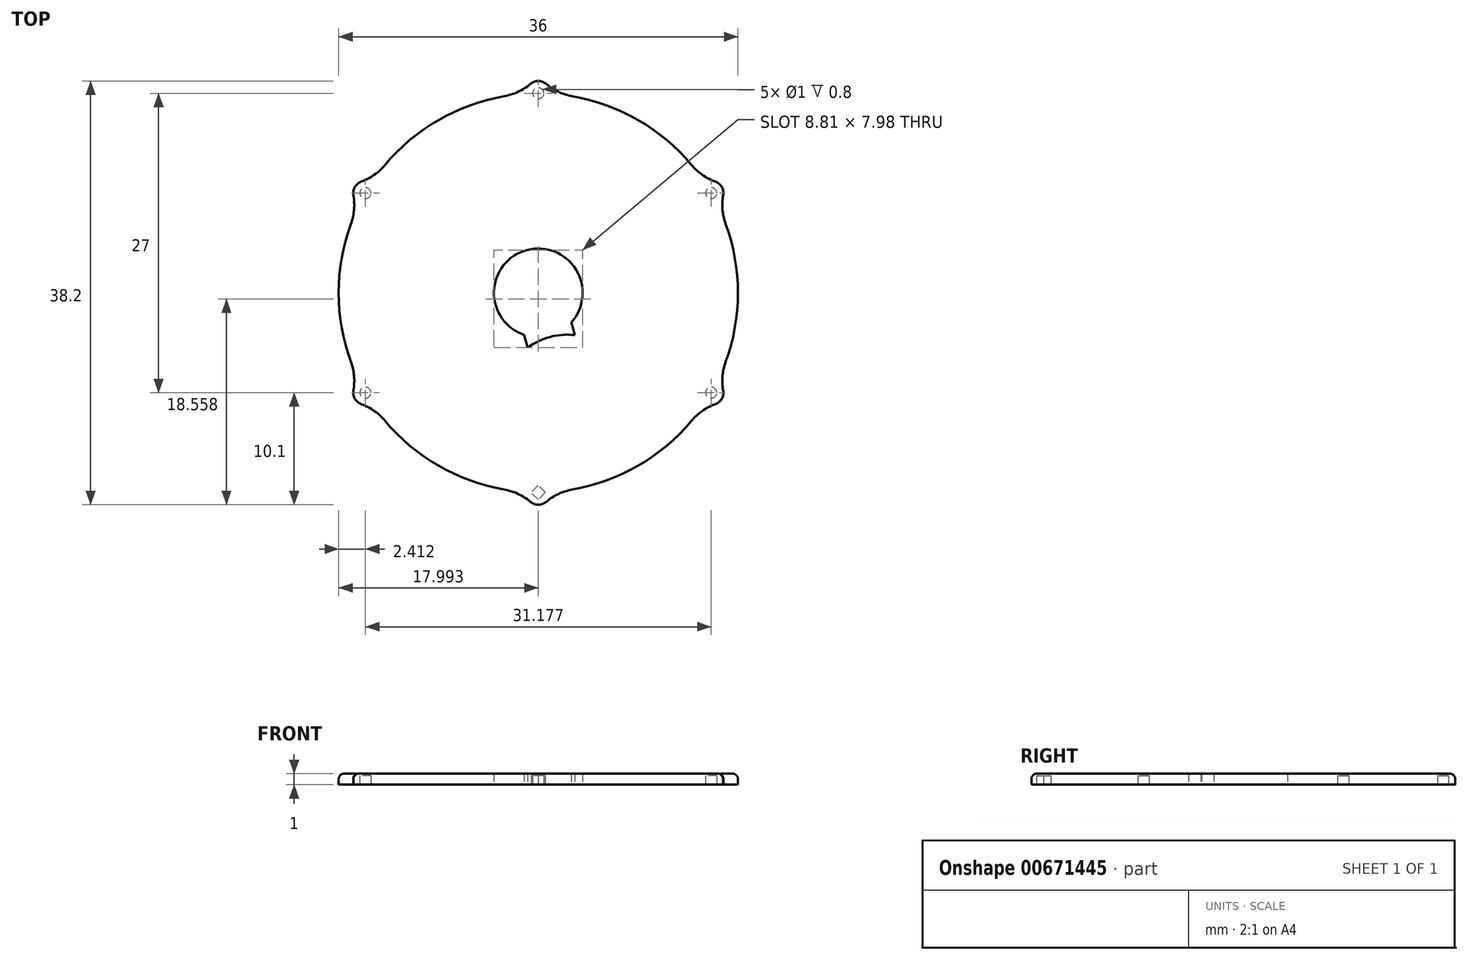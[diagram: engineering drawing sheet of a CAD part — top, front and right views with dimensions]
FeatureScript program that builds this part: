
annotation { "Feature Type Name" : "Feature", "Feature Type Description" : "" }
export const myFeature = defineFeature(function(context is Context, id is Id, definition is map)
    precondition{}
    {
        {
            var Q0;
            Q0=qCreatedBy(makeId("Top.planeOp"),FACE);
            var sketch = newSketch(context, id + "F0", { "sketchPlane" : qUnion([Q0])});
            skCircle(sketch, "E0", {"center": v(0, 0) * mm, "radius": 18 * mm});
            skCircle(sketch, "E1.0", {"center": v(0, 0) * mm, "radius": 17 * mm});
            skLineSegment(sketch, "E2.bottom", {"start": v(8.56, 15.83) * mm, "end": v(9.43, 15.33) * mm});
            skLineSegment(sketch, "E2.top", {"start": v(-9.43, -15.33) * mm, "end": v(-8.56, -15.83) * mm});
            skLineSegment(sketch, "E2.left", {"start": v(8.56, 15.83) * mm, "end": v(-9.43, -15.33) * mm});
            skLineSegment(sketch, "E2.right", {"start": v(9.43, 15.33) * mm, "end": v(-8.56, -15.83) * mm});
            skLineSegment(sketch, "E3.bottom", {"start": v(15.33, 9.43) * mm, "end": v(15.83, 8.56) * mm});
            skLineSegment(sketch, "E3.top", {"start": v(-15.83, -8.56) * mm, "end": v(-15.33, -9.43) * mm});
            skLineSegment(sketch, "E3.left", {"start": v(15.33, 9.43) * mm, "end": v(-15.83, -8.56) * mm});
            skLineSegment(sketch, "E3.right", {"start": v(15.83, 8.56) * mm, "end": v(-15.33, -9.43) * mm});
            skLineSegment(sketch, "E4", {"start": v(-38.35, 0) * mm, "end": v(39.17, 0) * mm, "construction": true});
            skLineSegment(sketch, "E5", {"start": v(0, 42.5) * mm, "end": v(0, -42.47) * mm, "construction": true});
            skLineSegment(sketch, "E6.bottom", {"start": v(-18, 0.5) * mm, "end": v(18, 0.5) * mm});
            skLineSegment(sketch, "E6.top", {"start": v(-18, -0.5) * mm, "end": v(18, -0.5) * mm});
            skLineSegment(sketch, "E6.left", {"start": v(-18, 0.5) * mm, "end": v(-18, -0.5) * mm});
            skLineSegment(sketch, "E6.right", {"start": v(18, 0.5) * mm, "end": v(18, -0.5) * mm});
            skLineSegment(sketch, "E7.bottom", {"start": v(-15.33, 9.43) * mm, "end": v(15.83, -8.56) * mm});
            skLineSegment(sketch, "E7.top", {"start": v(-15.83, 8.56) * mm, "end": v(15.33, -9.43) * mm});
            skLineSegment(sketch, "E7.left", {"start": v(-15.33, 9.43) * mm, "end": v(-15.83, 8.56) * mm});
            skLineSegment(sketch, "E7.right", {"start": v(15.83, -8.56) * mm, "end": v(15.33, -9.43) * mm});
            skLineSegment(sketch, "E8.bottom", {"start": v(-0.5, 18) * mm, "end": v(0.5, 18) * mm});
            skLineSegment(sketch, "E8.top", {"start": v(-0.5, -18) * mm, "end": v(0.5, -18) * mm});
            skLineSegment(sketch, "E8.left", {"start": v(-0.5, 18) * mm, "end": v(-0.5, -18) * mm});
            skLineSegment(sketch, "E8.right", {"start": v(0.5, 18) * mm, "end": v(0.5, -18) * mm});
            skLineSegment(sketch, "E9.bottom", {"start": v(-9.43, 15.33) * mm, "end": v(-8.56, 15.83) * mm});
            skLineSegment(sketch, "E9.top", {"start": v(8.56, -15.83) * mm, "end": v(9.43, -15.33) * mm});
            skLineSegment(sketch, "E9.left", {"start": v(-9.43, 15.33) * mm, "end": v(8.56, -15.83) * mm});
            skLineSegment(sketch, "E9.right", {"start": v(-8.56, 15.83) * mm, "end": v(9.43, -15.33) * mm});
            skCircle(sketch, "E10", {"center": v(0, 0) * mm, "radius": 13.47 * mm});
            skSolve(sketch);
        }
        {
            var Q0;
            Q0=qCreatedBy(makeId("Top.planeOp"),FACE);
            var sketch = newSketch(context, id + "F1", { "sketchPlane" : qUnion([Q0])});
            skCircle(sketch, "E11", {"center": v(0, 0) * mm, "radius": 18 * mm});
            skCircle(sketch, "E12", {"center": v(0, 0) * mm, "radius": 17 * mm});
            skSolve(sketch);
        }
        {
            var Q0;
            Q0=makeQuery(id+"F1.imprint","IMPRINT",FACE,{"disambiguationData":[TD([[makeQuery(id+"F1.imprint","IMPRINT",EDGE,{"derivedFrom":sQuery(id+"F1.wireOp",EDGE,"E11")}),1.0]])]});
            extrude(context, id + "F2", {"entities" : qUnion([Q0]), "depth" : 1 * mm, "offsetDistance" : 25 * mm});
        }
        {
            var Q0;
            Q0=makeQuery(id+"F1.imprint","IMPRINT",FACE,{"disambiguationData":[TD([[makeQuery(id+"F1.imprint","IMPRINT",EDGE,{"derivedFrom":sQuery(id+"F1.wireOp",EDGE,"E11")}),1.0]])]});
            var Q1;
            Q1=makeQuery(id+"F1.imprint","IMPRINT",FACE,{"disambiguationData":[TD([[makeQuery(id+"F1.imprint","IMPRINT",EDGE,{"derivedFrom":sQuery(id+"F1.wireOp",EDGE,"E12")}),1.0]])]});
            extrude(context, id + "F3", {"entities" : qUnion([Q0, Q1]), "operationType" : NewBodyOperationType.ADD, "depth" : 1 * mm, "offsetDistance" : 25 * mm});
        }
        {
            var Q0;
            Q0=qCreatedBy(makeId("Top.planeOp"),FACE);
            var sketch = newSketch(context, id + "F4", { "sketchPlane" : qUnion([Q0])});
            skCircle(sketch, "E13", {"center": v(0, 0) * mm, "radius": 18 * mm});
            skLineSegment(sketch, "E14", {"start": v(0, 18) * mm, "end": v(0, -18) * mm, "construction": true});
            skLineSegment(sketch, "E15", {"start": v(15.59, 9) * mm, "end": v(0, 0) * mm, "construction": true});
            skLineSegment(sketch, "E16", {"start": v(9, 15.59) * mm, "end": v(0, 0) * mm, "construction": true});
            skLineSegment(sketch, "E17", {"start": v(0, 0) * mm, "end": v(18, 0) * mm, "construction": true});
            skLineSegment(sketch, "E18", {"start": v(0, 0) * mm, "end": v(15.59, -9) * mm, "construction": true});
            skLineSegment(sketch, "E19", {"start": v(0, 0) * mm, "end": v(9, -15.59) * mm, "construction": true});
            skLineSegment(sketch, "E20", {"start": v(0, 0) * mm, "end": v(-9, 15.59) * mm, "construction": true});
            skLineSegment(sketch, "E21", {"start": v(0, 0) * mm, "end": v(-15.59, 9) * mm, "construction": true});
            skLineSegment(sketch, "E22", {"start": v(0, 0) * mm, "end": v(-18, 0) * mm, "construction": true});
            skLineSegment(sketch, "E23", {"start": v(0, 0) * mm, "end": v(-15.59, -9) * mm, "construction": true});
            skLineSegment(sketch, "E24", {"start": v(0, 0) * mm, "end": v(-9, -15.59) * mm, "construction": true});
            skCircle(sketch, "E25", {"center": v(0, 18) * mm, "radius": 1.1 * mm});
            skCircle(sketch, "E26", {"center": v(15.59, 9) * mm, "radius": 1.1 * mm});
            skCircle(sketch, "E27", {"center": v(15.59, -9) * mm, "radius": 1.1 * mm});
            skCircle(sketch, "E28", {"center": v(0, -18) * mm, "radius": 1.1 * mm});
            skCircle(sketch, "E29", {"center": v(-15.59, -9) * mm, "radius": 1.1 * mm});
            skCircle(sketch, "E30", {"center": v(-15.59, 9) * mm, "radius": 1.1 * mm});
            skCircle(sketch, "E31", {"center": v(-15.59, 9) * mm, "radius": 0.5 * mm});
            skCircle(sketch, "E32", {"center": v(0, 18) * mm, "radius": 0.5 * mm});
            skCircle(sketch, "E33", {"center": v(15.59, 9) * mm, "radius": 0.5 * mm});
            skCircle(sketch, "E34", {"center": v(15.59, -9) * mm, "radius": 0.5 * mm});
            skCircle(sketch, "E35", {"center": v(-15.59, -9) * mm, "radius": 0.5 * mm});
            skLineSegment(sketch, "E36.bottom", {"start": v(0.64, -18) * mm, "end": v(0, -18.64) * mm});
            skLineSegment(sketch, "E36.top", {"start": v(0, -17.36) * mm, "end": v(-0.64, -18) * mm});
            skLineSegment(sketch, "E36.left", {"start": v(0.64, -18) * mm, "end": v(0, -17.36) * mm});
            skLineSegment(sketch, "E36.right", {"start": v(0, -18.64) * mm, "end": v(-0.64, -18) * mm});
            skSolve(sketch);
        }
        {
            var Q0;
            {var subQ0=sQuery(id+"F4.wireOp",EDGE,"E30");var subQ1=sQuery(id+"F4.wireOp",EDGE,"E13");var subQ2=makeQuery(id+"F4.imprint","INTERSECT",VERTEX,{"disambiguationData":[OD(0.0)],"derivedFrom":[subQ1,subQ0]});Q0=makeQuery(id+"F4.imprint","IMPRINT",FACE,{"disambiguationData":[TD([[makeQuery(id+"F4.imprint","IMPRINT",EDGE,{"disambiguationData":[TD([[subQ2,-1.0]])],"derivedFrom":subQ1}),1.0]])]});}
            var Q1;
            {var subQ0=sQuery(id+"F4.wireOp",EDGE,"E30");var subQ1=sQuery(id+"F4.wireOp",EDGE,"E13");var subQ2=makeQuery(id+"F4.imprint","INTERSECT",VERTEX,{"disambiguationData":[OD(0.0)],"derivedFrom":[subQ1,subQ0]});Q1=makeQuery(id+"F4.imprint","IMPRINT",FACE,{"disambiguationData":[TD([[makeQuery(id+"F4.imprint","IMPRINT",EDGE,{"disambiguationData":[TD([[subQ2,-1.0]])],"derivedFrom":subQ1}),-1.0]])]});}
            var Q2;
            {var subQ0=sQuery(id+"F4.wireOp",EDGE,"E25");var subQ1=sQuery(id+"F4.wireOp",EDGE,"E13");var subQ2=makeQuery(id+"F4.imprint","INTERSECT",VERTEX,{"disambiguationData":[OD(0.0)],"derivedFrom":[subQ1,subQ0]});Q2=makeQuery(id+"F4.imprint","IMPRINT",FACE,{"disambiguationData":[TD([[makeQuery(id+"F4.imprint","IMPRINT",EDGE,{"disambiguationData":[TD([[subQ2,-1.0]])],"derivedFrom":subQ1}),1.0]])]});}
            var Q3;
            {var subQ0=sQuery(id+"F4.wireOp",EDGE,"E25");var subQ1=sQuery(id+"F4.wireOp",EDGE,"E13");var subQ2=makeQuery(id+"F4.imprint","INTERSECT",VERTEX,{"disambiguationData":[OD(0.0)],"derivedFrom":[subQ1,subQ0]});Q3=makeQuery(id+"F4.imprint","IMPRINT",FACE,{"disambiguationData":[TD([[makeQuery(id+"F4.imprint","IMPRINT",EDGE,{"disambiguationData":[TD([[subQ2,-1.0]])],"derivedFrom":subQ1}),-1.0]])]});}
            var Q4;
            {var subQ0=sQuery(id+"F4.wireOp",EDGE,"E26");var subQ1=sQuery(id+"F4.wireOp",EDGE,"E13");var subQ2=makeQuery(id+"F4.imprint","INTERSECT",VERTEX,{"disambiguationData":[OD(0.0)],"derivedFrom":[subQ1,subQ0]});Q4=makeQuery(id+"F4.imprint","IMPRINT",FACE,{"disambiguationData":[TD([[makeQuery(id+"F4.imprint","IMPRINT",EDGE,{"disambiguationData":[TD([[subQ2,-1.0]])],"derivedFrom":subQ1}),-1.0]])]});}
            var Q5;
            {var subQ0=sQuery(id+"F4.wireOp",EDGE,"E26");var subQ1=sQuery(id+"F4.wireOp",EDGE,"E13");var subQ2=makeQuery(id+"F4.imprint","INTERSECT",VERTEX,{"disambiguationData":[OD(0.0)],"derivedFrom":[subQ1,subQ0]});Q5=makeQuery(id+"F4.imprint","IMPRINT",FACE,{"disambiguationData":[TD([[makeQuery(id+"F4.imprint","IMPRINT",EDGE,{"disambiguationData":[TD([[subQ2,-1.0]])],"derivedFrom":subQ1}),1.0]])]});}
            var Q6;
            {var subQ0=sQuery(id+"F4.wireOp",EDGE,"E29");var subQ1=sQuery(id+"F4.wireOp",EDGE,"E13");var subQ2=makeQuery(id+"F4.imprint","INTERSECT",VERTEX,{"disambiguationData":[OD(0.0)],"derivedFrom":[subQ1,subQ0]});Q6=makeQuery(id+"F4.imprint","IMPRINT",FACE,{"disambiguationData":[TD([[makeQuery(id+"F4.imprint","IMPRINT",EDGE,{"disambiguationData":[TD([[subQ2,-1.0]])],"derivedFrom":subQ1}),1.0]])]});}
            var Q7;
            {var subQ0=sQuery(id+"F4.wireOp",EDGE,"E29");var subQ1=sQuery(id+"F4.wireOp",EDGE,"E13");var subQ2=makeQuery(id+"F4.imprint","INTERSECT",VERTEX,{"disambiguationData":[OD(0.0)],"derivedFrom":[subQ1,subQ0]});Q7=makeQuery(id+"F4.imprint","IMPRINT",FACE,{"disambiguationData":[TD([[makeQuery(id+"F4.imprint","IMPRINT",EDGE,{"disambiguationData":[TD([[subQ2,-1.0]])],"derivedFrom":subQ1}),-1.0]])]});}
            var Q8;
            {var subQ3=sQuery(id+"F4.wireOp",EDGE,"E13");var subQ5=sQuery(id+"F4.wireOp",EDGE,"E28");var subQ6=makeQuery(id+"F4.imprint","INTERSECT",VERTEX,{"disambiguationData":[OD(0.0)],"derivedFrom":[subQ3,subQ5]});Q8=makeQuery(id+"F4.imprint","IMPRINT",FACE,{"disambiguationData":[TD([[makeQuery(id+"F4.imprint","IMPRINT",EDGE,{"disambiguationData":[TD([[subQ6,-1.0]])],"derivedFrom":subQ3}),1.0]])]});}
            var Q9;
            {var subQ6=sQuery(id+"F4.wireOp",EDGE,"E36.bottom");Q9=makeQuery(id+"F4.imprint","IMPRINT",FACE,{"disambiguationData":[TD([[makeQuery(id+"F4.imprint","IMPRINT",EDGE,{"derivedFrom":subQ6}),1.0]])]});}
            var Q10;
            {var subQ0=sQuery(id+"F4.wireOp",EDGE,"E27");var subQ1=sQuery(id+"F4.wireOp",EDGE,"E13");var subQ2=makeQuery(id+"F4.imprint","INTERSECT",VERTEX,{"disambiguationData":[OD(0.0)],"derivedFrom":[subQ1,subQ0]});Q10=makeQuery(id+"F4.imprint","IMPRINT",FACE,{"disambiguationData":[TD([[makeQuery(id+"F4.imprint","IMPRINT",EDGE,{"disambiguationData":[TD([[subQ2,-1.0]])],"derivedFrom":subQ1}),-1.0]])]});}
            var Q11;
            {var subQ0=sQuery(id+"F4.wireOp",EDGE,"E27");var subQ1=sQuery(id+"F4.wireOp",EDGE,"E13");var subQ2=makeQuery(id+"F4.imprint","INTERSECT",VERTEX,{"disambiguationData":[OD(0.0)],"derivedFrom":[subQ1,subQ0]});Q11=makeQuery(id+"F4.imprint","IMPRINT",FACE,{"disambiguationData":[TD([[makeQuery(id+"F4.imprint","IMPRINT",EDGE,{"disambiguationData":[TD([[subQ2,-1.0]])],"derivedFrom":subQ1}),1.0]])]});}
            var Q12;
            {var subQ0=sQuery(id+"F4.wireOp",EDGE,"E31");var subQ1=sQuery(id+"F4.wireOp",EDGE,"E13");var subQ2=makeQuery(id+"F4.imprint","INTERSECT",VERTEX,{"disambiguationData":[OD(0.0)],"derivedFrom":[subQ1,subQ0]});Q12=makeQuery(id+"F4.imprint","IMPRINT",FACE,{"disambiguationData":[TD([[makeQuery(id+"F4.imprint","IMPRINT",EDGE,{"disambiguationData":[TD([[subQ2,-1.0]])],"derivedFrom":subQ1}),1.0]])]});}
            var Q13;
            {var subQ0=sQuery(id+"F4.wireOp",EDGE,"E31");var subQ1=sQuery(id+"F4.wireOp",EDGE,"E13");var subQ2=makeQuery(id+"F4.imprint","INTERSECT",VERTEX,{"disambiguationData":[OD(0.0)],"derivedFrom":[subQ1,subQ0]});Q13=makeQuery(id+"F4.imprint","IMPRINT",FACE,{"disambiguationData":[TD([[makeQuery(id+"F4.imprint","IMPRINT",EDGE,{"disambiguationData":[TD([[subQ2,-1.0]])],"derivedFrom":subQ1}),-1.0]])]});}
            var Q14;
            {var subQ0=sQuery(id+"F4.wireOp",EDGE,"E32");var subQ1=sQuery(id+"F4.wireOp",EDGE,"E13");var subQ2=makeQuery(id+"F4.imprint","INTERSECT",VERTEX,{"disambiguationData":[OD(0.0)],"derivedFrom":[subQ1,subQ0]});Q14=makeQuery(id+"F4.imprint","IMPRINT",FACE,{"disambiguationData":[TD([[makeQuery(id+"F4.imprint","IMPRINT",EDGE,{"disambiguationData":[TD([[subQ2,-1.0]])],"derivedFrom":subQ1}),-1.0]])]});}
            var Q15;
            {var subQ0=sQuery(id+"F4.wireOp",EDGE,"E32");var subQ1=sQuery(id+"F4.wireOp",EDGE,"E13");var subQ2=makeQuery(id+"F4.imprint","INTERSECT",VERTEX,{"disambiguationData":[OD(0.0)],"derivedFrom":[subQ1,subQ0]});Q15=makeQuery(id+"F4.imprint","IMPRINT",FACE,{"disambiguationData":[TD([[makeQuery(id+"F4.imprint","IMPRINT",EDGE,{"disambiguationData":[TD([[subQ2,-1.0]])],"derivedFrom":subQ1}),1.0]])]});}
            var Q16;
            {var subQ0=sQuery(id+"F4.wireOp",EDGE,"E33");var subQ1=sQuery(id+"F4.wireOp",EDGE,"E13");var subQ2=makeQuery(id+"F4.imprint","INTERSECT",VERTEX,{"disambiguationData":[OD(0.0)],"derivedFrom":[subQ1,subQ0]});Q16=makeQuery(id+"F4.imprint","IMPRINT",FACE,{"disambiguationData":[TD([[makeQuery(id+"F4.imprint","IMPRINT",EDGE,{"disambiguationData":[TD([[subQ2,-1.0]])],"derivedFrom":subQ1}),-1.0]])]});}
            var Q17;
            {var subQ0=sQuery(id+"F4.wireOp",EDGE,"E33");var subQ1=sQuery(id+"F4.wireOp",EDGE,"E13");var subQ2=makeQuery(id+"F4.imprint","INTERSECT",VERTEX,{"disambiguationData":[OD(0.0)],"derivedFrom":[subQ1,subQ0]});Q17=makeQuery(id+"F4.imprint","IMPRINT",FACE,{"disambiguationData":[TD([[makeQuery(id+"F4.imprint","IMPRINT",EDGE,{"disambiguationData":[TD([[subQ2,-1.0]])],"derivedFrom":subQ1}),1.0]])]});}
            var Q18;
            {var subQ0=sQuery(id+"F4.wireOp",EDGE,"E34");var subQ1=sQuery(id+"F4.wireOp",EDGE,"E13");var subQ2=makeQuery(id+"F4.imprint","INTERSECT",VERTEX,{"disambiguationData":[OD(0.0)],"derivedFrom":[subQ1,subQ0]});Q18=makeQuery(id+"F4.imprint","IMPRINT",FACE,{"disambiguationData":[TD([[makeQuery(id+"F4.imprint","IMPRINT",EDGE,{"disambiguationData":[TD([[subQ2,-1.0]])],"derivedFrom":subQ1}),-1.0]])]});}
            var Q19;
            {var subQ0=sQuery(id+"F4.wireOp",EDGE,"E34");var subQ1=sQuery(id+"F4.wireOp",EDGE,"E13");var subQ2=makeQuery(id+"F4.imprint","INTERSECT",VERTEX,{"disambiguationData":[OD(0.0)],"derivedFrom":[subQ1,subQ0]});Q19=makeQuery(id+"F4.imprint","IMPRINT",FACE,{"disambiguationData":[TD([[makeQuery(id+"F4.imprint","IMPRINT",EDGE,{"disambiguationData":[TD([[subQ2,-1.0]])],"derivedFrom":subQ1}),1.0]])]});}
            var Q20;
            {var subQ1=sQuery(id+"F4.wireOp",EDGE,"E36.bottom");Q20=makeQuery(id+"F4.imprint","IMPRINT",FACE,{"disambiguationData":[TD([[makeQuery(id+"F4.imprint","IMPRINT",EDGE,{"derivedFrom":subQ1}),-1.0]])]});}
            var Q21;
            {var subQ0=sQuery(id+"F4.wireOp",EDGE,"E35");var subQ1=sQuery(id+"F4.wireOp",EDGE,"E13");var subQ2=makeQuery(id+"F4.imprint","INTERSECT",VERTEX,{"disambiguationData":[OD(0.0)],"derivedFrom":[subQ1,subQ0]});Q21=makeQuery(id+"F4.imprint","IMPRINT",FACE,{"disambiguationData":[TD([[makeQuery(id+"F4.imprint","IMPRINT",EDGE,{"disambiguationData":[TD([[subQ2,-1.0]])],"derivedFrom":subQ1}),-1.0]])]});}
            var Q22;
            {var subQ0=sQuery(id+"F4.wireOp",EDGE,"E35");var subQ1=sQuery(id+"F4.wireOp",EDGE,"E13");var subQ2=makeQuery(id+"F4.imprint","INTERSECT",VERTEX,{"disambiguationData":[OD(0.0)],"derivedFrom":[subQ1,subQ0]});Q22=makeQuery(id+"F4.imprint","IMPRINT",FACE,{"disambiguationData":[TD([[makeQuery(id+"F4.imprint","IMPRINT",EDGE,{"disambiguationData":[TD([[subQ2,-1.0]])],"derivedFrom":subQ1}),1.0]])]});}
            var Q23;
            {var subQ0=sQuery(id+"F4.wireOp",EDGE,"E36.top");var subQ1=sQuery(id+"F4.wireOp",EDGE,"E13");var subQ2=makeQuery(id+"F4.imprint","INTERSECT",VERTEX,{"derivedFrom":[subQ1,subQ0]});Q23=makeQuery(id+"F4.imprint","IMPRINT",FACE,{"disambiguationData":[TD([[makeQuery(id+"F4.imprint","IMPRINT",EDGE,{"disambiguationData":[TD([[subQ2,-1.0]])],"derivedFrom":subQ1}),1.0]])]});}
            extrude(context, id + "F5", {"entities" : qUnion([Q0, Q1, Q2, Q3, Q4, Q5, Q6, Q7, Q8, Q9, Q10, Q11, Q12, Q13, Q14, Q15, Q16, Q17, Q18, Q19, Q20, Q21, Q22, Q23]), "operationType" : NewBodyOperationType.ADD, "depth" : 1 * mm, "offsetDistance" : 25 * mm});
        }
        {
            var Q0;
            Q0=makeQuery(id+"F5.boolean.opBoolean","INTERSECT",EDGE,{"disambiguationData":[OD(0.0)],"derivedFrom":[makeQuery(id+"F2.opExtrude","SWEPT_FACE",FACE,{"disambiguationData":[OSD([sQuery(id+"F1.wireOp",EDGE,"E11")])]}),makeQuery(id+"F5.opExtrude","SWEPT_FACE",FACE,{"disambiguationData":[OSD([sQuery(id+"F4.wireOp",EDGE,"E30")])]})]});
            var Q1;
            Q1=makeQuery(id+"F5.boolean.opBoolean","INTERSECT",EDGE,{"disambiguationData":[OD(1.0)],"derivedFrom":[makeQuery(id+"F2.opExtrude","SWEPT_FACE",FACE,{"disambiguationData":[OSD([sQuery(id+"F1.wireOp",EDGE,"E11")])]}),makeQuery(id+"F5.opExtrude","SWEPT_FACE",FACE,{"disambiguationData":[OSD([sQuery(id+"F4.wireOp",EDGE,"E30")])]})]});
            var Q2;
            Q2=makeQuery(id+"F5.boolean.opBoolean","INTERSECT",EDGE,{"disambiguationData":[OD(1.0)],"derivedFrom":[makeQuery(id+"F2.opExtrude","SWEPT_FACE",FACE,{"disambiguationData":[OSD([sQuery(id+"F1.wireOp",EDGE,"E11")])]}),makeQuery(id+"F5.opExtrude","SWEPT_FACE",FACE,{"disambiguationData":[OSD([sQuery(id+"F4.wireOp",EDGE,"E25")])]})]});
            var Q3;
            Q3=makeQuery(id+"F5.boolean.opBoolean","INTERSECT",EDGE,{"disambiguationData":[OD(1.0)],"derivedFrom":[makeQuery(id+"F2.opExtrude","SWEPT_FACE",FACE,{"disambiguationData":[OSD([sQuery(id+"F1.wireOp",EDGE,"E11")])]}),makeQuery(id+"F5.opExtrude","SWEPT_FACE",FACE,{"disambiguationData":[OSD([sQuery(id+"F4.wireOp",EDGE,"E29")])]})]});
            var Q4;
            Q4=makeQuery(id+"F5.boolean.opBoolean","INTERSECT",EDGE,{"disambiguationData":[OD(0.0)],"derivedFrom":[makeQuery(id+"F2.opExtrude","SWEPT_FACE",FACE,{"disambiguationData":[OSD([sQuery(id+"F1.wireOp",EDGE,"E11")])]}),makeQuery(id+"F5.opExtrude","SWEPT_FACE",FACE,{"disambiguationData":[OSD([sQuery(id+"F4.wireOp",EDGE,"E29")])]})]});
            var Q5;
            Q5=makeQuery(id+"F5.boolean.opBoolean","INTERSECT",EDGE,{"disambiguationData":[OD(1.0)],"derivedFrom":[makeQuery(id+"F2.opExtrude","SWEPT_FACE",FACE,{"disambiguationData":[OSD([sQuery(id+"F1.wireOp",EDGE,"E11")])]}),makeQuery(id+"F5.opExtrude","SWEPT_FACE",FACE,{"disambiguationData":[OSD([sQuery(id+"F4.wireOp",EDGE,"E28")])]})]});
            var Q6;
            Q6=makeQuery(id+"F5.boolean.opBoolean","INTERSECT",EDGE,{"disambiguationData":[OD(0.0)],"derivedFrom":[makeQuery(id+"F2.opExtrude","SWEPT_FACE",FACE,{"disambiguationData":[OSD([sQuery(id+"F1.wireOp",EDGE,"E11")])]}),makeQuery(id+"F5.opExtrude","SWEPT_FACE",FACE,{"disambiguationData":[OSD([sQuery(id+"F4.wireOp",EDGE,"E28")])]})]});
            var Q7;
            Q7=makeQuery(id+"F5.boolean.opBoolean","INTERSECT",EDGE,{"disambiguationData":[OD(1.0)],"derivedFrom":[makeQuery(id+"F2.opExtrude","SWEPT_FACE",FACE,{"disambiguationData":[OSD([sQuery(id+"F1.wireOp",EDGE,"E11")])]}),makeQuery(id+"F5.opExtrude","SWEPT_FACE",FACE,{"disambiguationData":[OSD([sQuery(id+"F4.wireOp",EDGE,"E27")])]})]});
            var Q8;
            Q8=makeQuery(id+"F5.boolean.opBoolean","INTERSECT",EDGE,{"disambiguationData":[OD(0.0)],"derivedFrom":[makeQuery(id+"F2.opExtrude","SWEPT_FACE",FACE,{"disambiguationData":[OSD([sQuery(id+"F1.wireOp",EDGE,"E11")])]}),makeQuery(id+"F5.opExtrude","SWEPT_FACE",FACE,{"disambiguationData":[OSD([sQuery(id+"F4.wireOp",EDGE,"E27")])]})]});
            var Q9;
            Q9=makeQuery(id+"F5.boolean.opBoolean","INTERSECT",EDGE,{"disambiguationData":[OD(1.0)],"derivedFrom":[makeQuery(id+"F2.opExtrude","SWEPT_FACE",FACE,{"disambiguationData":[OSD([sQuery(id+"F1.wireOp",EDGE,"E11")])]}),makeQuery(id+"F5.opExtrude","SWEPT_FACE",FACE,{"disambiguationData":[OSD([sQuery(id+"F4.wireOp",EDGE,"E26")])]})]});
            var Q10;
            Q10=makeQuery(id+"F5.boolean.opBoolean","INTERSECT",EDGE,{"disambiguationData":[OD(0.0)],"derivedFrom":[makeQuery(id+"F2.opExtrude","SWEPT_FACE",FACE,{"disambiguationData":[OSD([sQuery(id+"F1.wireOp",EDGE,"E11")])]}),makeQuery(id+"F5.opExtrude","SWEPT_FACE",FACE,{"disambiguationData":[OSD([sQuery(id+"F4.wireOp",EDGE,"E26")])]})]});
            var Q11;
            Q11=makeQuery(id+"F5.boolean.opBoolean","INTERSECT",EDGE,{"disambiguationData":[OD(0.0)],"derivedFrom":[makeQuery(id+"F2.opExtrude","SWEPT_FACE",FACE,{"disambiguationData":[OSD([sQuery(id+"F1.wireOp",EDGE,"E11")])]}),makeQuery(id+"F5.opExtrude","SWEPT_FACE",FACE,{"disambiguationData":[OSD([sQuery(id+"F4.wireOp",EDGE,"E25")])]})]});
            fillet(context, id + "F6", {"entities" : qUnion([Q0, Q1, Q2, Q3, Q4, Q5, Q6, Q7, Q8, Q9, Q10, Q11]), "radius" : 5 * mm, "tangentPropagation" : true, "allowEdgeOverflow" : false});
        }
        {
            var Q0;
            {var subQ0=sQuery(id+"F4.wireOp",EDGE,"E31");var subQ1=sQuery(id+"F4.wireOp",EDGE,"E13");var subQ2=makeQuery(id+"F4.imprint","INTERSECT",VERTEX,{"disambiguationData":[OD(0.0)],"derivedFrom":[subQ1,subQ0]});Q0=makeQuery(id+"F4.imprint","IMPRINT",FACE,{"disambiguationData":[TD([[makeQuery(id+"F4.imprint","IMPRINT",EDGE,{"disambiguationData":[TD([[subQ2,-1.0]])],"derivedFrom":subQ1}),-1.0]])]});}
            var Q1;
            {var subQ0=sQuery(id+"F4.wireOp",EDGE,"E31");var subQ1=sQuery(id+"F4.wireOp",EDGE,"E13");var subQ2=makeQuery(id+"F4.imprint","INTERSECT",VERTEX,{"disambiguationData":[OD(0.0)],"derivedFrom":[subQ1,subQ0]});Q1=makeQuery(id+"F4.imprint","IMPRINT",FACE,{"disambiguationData":[TD([[makeQuery(id+"F4.imprint","IMPRINT",EDGE,{"disambiguationData":[TD([[subQ2,-1.0]])],"derivedFrom":subQ1}),1.0]])]});}
            var Q2;
            {var subQ0=sQuery(id+"F4.wireOp",EDGE,"E32");var subQ1=sQuery(id+"F4.wireOp",EDGE,"E13");var subQ2=makeQuery(id+"F4.imprint","INTERSECT",VERTEX,{"disambiguationData":[OD(0.0)],"derivedFrom":[subQ1,subQ0]});Q2=makeQuery(id+"F4.imprint","IMPRINT",FACE,{"disambiguationData":[TD([[makeQuery(id+"F4.imprint","IMPRINT",EDGE,{"disambiguationData":[TD([[subQ2,-1.0]])],"derivedFrom":subQ1}),-1.0]])]});}
            var Q3;
            {var subQ0=sQuery(id+"F4.wireOp",EDGE,"E32");var subQ1=sQuery(id+"F4.wireOp",EDGE,"E13");var subQ2=makeQuery(id+"F4.imprint","INTERSECT",VERTEX,{"disambiguationData":[OD(0.0)],"derivedFrom":[subQ1,subQ0]});Q3=makeQuery(id+"F4.imprint","IMPRINT",FACE,{"disambiguationData":[TD([[makeQuery(id+"F4.imprint","IMPRINT",EDGE,{"disambiguationData":[TD([[subQ2,-1.0]])],"derivedFrom":subQ1}),1.0]])]});}
            var Q4;
            {var subQ0=sQuery(id+"F4.wireOp",EDGE,"E33");var subQ1=sQuery(id+"F4.wireOp",EDGE,"E13");var subQ2=makeQuery(id+"F4.imprint","INTERSECT",VERTEX,{"disambiguationData":[OD(0.0)],"derivedFrom":[subQ1,subQ0]});Q4=makeQuery(id+"F4.imprint","IMPRINT",FACE,{"disambiguationData":[TD([[makeQuery(id+"F4.imprint","IMPRINT",EDGE,{"disambiguationData":[TD([[subQ2,-1.0]])],"derivedFrom":subQ1}),1.0]])]});}
            var Q5;
            {var subQ0=sQuery(id+"F4.wireOp",EDGE,"E33");var subQ1=sQuery(id+"F4.wireOp",EDGE,"E13");var subQ2=makeQuery(id+"F4.imprint","INTERSECT",VERTEX,{"disambiguationData":[OD(0.0)],"derivedFrom":[subQ1,subQ0]});Q5=makeQuery(id+"F4.imprint","IMPRINT",FACE,{"disambiguationData":[TD([[makeQuery(id+"F4.imprint","IMPRINT",EDGE,{"disambiguationData":[TD([[subQ2,-1.0]])],"derivedFrom":subQ1}),-1.0]])]});}
            var Q6;
            {var subQ0=sQuery(id+"F4.wireOp",EDGE,"E34");var subQ1=sQuery(id+"F4.wireOp",EDGE,"E13");var subQ2=makeQuery(id+"F4.imprint","INTERSECT",VERTEX,{"disambiguationData":[OD(0.0)],"derivedFrom":[subQ1,subQ0]});Q6=makeQuery(id+"F4.imprint","IMPRINT",FACE,{"disambiguationData":[TD([[makeQuery(id+"F4.imprint","IMPRINT",EDGE,{"disambiguationData":[TD([[subQ2,-1.0]])],"derivedFrom":subQ1}),1.0]])]});}
            var Q7;
            {var subQ0=sQuery(id+"F4.wireOp",EDGE,"E34");var subQ1=sQuery(id+"F4.wireOp",EDGE,"E13");var subQ2=makeQuery(id+"F4.imprint","INTERSECT",VERTEX,{"disambiguationData":[OD(0.0)],"derivedFrom":[subQ1,subQ0]});Q7=makeQuery(id+"F4.imprint","IMPRINT",FACE,{"disambiguationData":[TD([[makeQuery(id+"F4.imprint","IMPRINT",EDGE,{"disambiguationData":[TD([[subQ2,-1.0]])],"derivedFrom":subQ1}),-1.0]])]});}
            var Q8;
            {var subQ1=sQuery(id+"F4.wireOp",EDGE,"E36.bottom");Q8=makeQuery(id+"F4.imprint","IMPRINT",FACE,{"disambiguationData":[TD([[makeQuery(id+"F4.imprint","IMPRINT",EDGE,{"derivedFrom":subQ1}),-1.0]])]});}
            var Q9;
            {var subQ0=sQuery(id+"F4.wireOp",EDGE,"E36.top");var subQ1=sQuery(id+"F4.wireOp",EDGE,"E13");var subQ2=makeQuery(id+"F4.imprint","INTERSECT",VERTEX,{"derivedFrom":[subQ1,subQ0]});Q9=makeQuery(id+"F4.imprint","IMPRINT",FACE,{"disambiguationData":[TD([[makeQuery(id+"F4.imprint","IMPRINT",EDGE,{"disambiguationData":[TD([[subQ2,-1.0]])],"derivedFrom":subQ1}),1.0]])]});}
            var Q10;
            {var subQ0=sQuery(id+"F4.wireOp",EDGE,"E35");var subQ1=sQuery(id+"F4.wireOp",EDGE,"E13");var subQ2=makeQuery(id+"F4.imprint","INTERSECT",VERTEX,{"disambiguationData":[OD(0.0)],"derivedFrom":[subQ1,subQ0]});Q10=makeQuery(id+"F4.imprint","IMPRINT",FACE,{"disambiguationData":[TD([[makeQuery(id+"F4.imprint","IMPRINT",EDGE,{"disambiguationData":[TD([[subQ2,-1.0]])],"derivedFrom":subQ1}),-1.0]])]});}
            var Q11;
            {var subQ0=sQuery(id+"F4.wireOp",EDGE,"E35");var subQ1=sQuery(id+"F4.wireOp",EDGE,"E13");var subQ2=makeQuery(id+"F4.imprint","INTERSECT",VERTEX,{"disambiguationData":[OD(0.0)],"derivedFrom":[subQ1,subQ0]});Q11=makeQuery(id+"F4.imprint","IMPRINT",FACE,{"disambiguationData":[TD([[makeQuery(id+"F4.imprint","IMPRINT",EDGE,{"disambiguationData":[TD([[subQ2,-1.0]])],"derivedFrom":subQ1}),1.0]])]});}
            extrude(context, id + "F7", {"entities" : qUnion([Q0, Q1, Q2, Q3, Q4, Q5, Q6, Q7, Q8, Q9, Q10, Q11]), "operationType" : NewBodyOperationType.REMOVE, "depth" : .8 * mm, "offsetDistance" : 25 * mm});
        }
        {
            var Q0;
            Q0=qCreatedBy(makeId("Top.planeOp"),FACE);
            var sketch = newSketch(context, id + "F8", { "sketchPlane" : qUnion([Q0])});
            skCircle(sketch, "E37", {"center": v(0, 0) * mm, "radius": 4 * mm});
            skLineSegment(sketch, "E38", {"start": v(0, 0) * mm, "end": v(4.14, -15.45) * mm});
            skLineSegment(sketch, "E39.0", {"start": v(-2.13, -0.57) * mm, "end": v(2.25, -16.89) * mm});
            skLineSegment(sketch, "E40.0", {"start": v(2.13, 0.57) * mm, "end": v(6.5, -15.78) * mm});
            skCircle(sketch, "E41", {"center": v(2.6, -9.71) * mm, "radius": 5.95 * mm});
            skSolve(sketch);
        }
        {
            var Q0;
            {var subQ0=sQuery(id+"F8.wireOp",EDGE,"E37");var subQ1=makeQuery(id+"F8.imprint","INTERSECT",VERTEX,{"derivedFrom":[subQ0,sQuery(id+"F8.wireOp",EDGE,"E39.0")]});Q0=makeQuery(id+"F8.imprint","IMPRINT",FACE,{"disambiguationData":[TD([[makeQuery(id+"F8.imprint","IMPRINT",EDGE,{"disambiguationData":[TD([[subQ1,-1.0]])],"derivedFrom":subQ0}),1.0]])]});}
            var Q1;
            {var subQ0=sQuery(id+"F8.wireOp",EDGE,"E39.0");var subQ1=sQuery(id+"F8.wireOp",EDGE,"E37");var subQ2=makeQuery(id+"F8.imprint","INTERSECT",VERTEX,{"derivedFrom":[subQ1,subQ0]});Q1=makeQuery(id+"F8.imprint","IMPRINT",FACE,{"disambiguationData":[TD([[makeQuery(id+"F8.imprint","IMPRINT",EDGE,{"disambiguationData":[TD([[subQ2,-1.0]])],"derivedFrom":subQ1}),-1.0]])]});}
            var Q2;
            {var subQ0=sQuery(id+"F8.wireOp",EDGE,"E40.0");var subQ1=sQuery(id+"F8.wireOp",EDGE,"E37");var subQ2=makeQuery(id+"F8.imprint","INTERSECT",VERTEX,{"derivedFrom":[subQ1,subQ0]});Q2=makeQuery(id+"F8.imprint","IMPRINT",FACE,{"disambiguationData":[TD([[makeQuery(id+"F8.imprint","IMPRINT",EDGE,{"disambiguationData":[TD([[subQ2,1.0]])],"derivedFrom":subQ1}),-1.0]])]});}
            var Q3;
            {var subQ0=sQuery(id+"F8.wireOp",EDGE,"E41");var subQ1=sQuery(id+"F8.wireOp",EDGE,"E38");var subQ2=makeQuery(id+"F8.imprint","INTERSECT",VERTEX,{"disambiguationData":[OD(0.0)],"derivedFrom":[subQ1,subQ0]});Q3=makeQuery(id+"F8.imprint","IMPRINT",FACE,{"disambiguationData":[TD([[makeQuery(id+"F8.imprint","IMPRINT",EDGE,{"disambiguationData":[TD([[subQ2,1.0]])],"derivedFrom":subQ1}),1.0]])]});}
            var Q4;
            {var subQ0=sQuery(id+"F8.wireOp",EDGE,"E41");var subQ1=sQuery(id+"F8.wireOp",EDGE,"E38");var subQ2=makeQuery(id+"F8.imprint","INTERSECT",VERTEX,{"disambiguationData":[OD(0.0)],"derivedFrom":[subQ1,subQ0]});Q4=makeQuery(id+"F8.imprint","IMPRINT",FACE,{"disambiguationData":[TD([[makeQuery(id+"F8.imprint","IMPRINT",EDGE,{"disambiguationData":[TD([[subQ2,1.0]])],"derivedFrom":subQ1}),-1.0]])]});}
            extrude(context, id + "F9", {"entities" : qUnion([Q0, Q1, Q2, Q3, Q4]), "operationType" : NewBodyOperationType.REMOVE, "depth" : 1 * mm, "offsetDistance" : 25 * mm});
        }
        {
            var Q0;
            {var subQ0=sQuery(id+"F4.wireOp",EDGE,"E28");var subQ1=sQuery(id+"F4.wireOp",EDGE,"E27");var subQ2=sQuery(id+"F1.wireOp",EDGE,"E11");Q0=makeQuery(id+"F5.boolean.opBoolean","SPLIT",EDGE,{"disambiguationData":[TD([makeQuery(id+"F2.opExtrude","SWEPT_FACE",FACE,{"disambiguationData":[OSD([subQ2])]}),makeQuery(id+"F2.opExtrude","CAP_FACE",FACE,{"disambiguationData":[OSD([subQ2,sQuery(id+"F1.wireOp",EDGE,"E12")])],"isStart":false}),makeQuery(id+"F3.opExtrude","CAP_FACE",FACE,{"disambiguationData":[OSD([subQ2])],"isStart":false}),makeQuery(id+"F5.opExtrude","CAP_FACE",FACE,{"disambiguationData":[OSD([sQuery(id+"F4.wireOp",EDGE,"E25")])],"isStart":false}),makeQuery(id+"F5.opExtrude","CAP_FACE",FACE,{"disambiguationData":[OSD([sQuery(id+"F4.wireOp",EDGE,"E26")])],"isStart":false}),makeQuery(id+"F5.opExtrude","SWEPT_FACE",FACE,{"disambiguationData":[OSD([subQ1])]}),makeQuery(id+"F5.opExtrude","CAP_FACE",FACE,{"disambiguationData":[OSD([subQ1])],"isStart":false}),makeQuery(id+"F5.opExtrude","SWEPT_FACE",FACE,{"disambiguationData":[OSD([subQ0])]}),makeQuery(id+"F5.opExtrude","CAP_FACE",FACE,{"disambiguationData":[OSD([subQ0])],"isStart":false}),makeQuery(id+"F5.opExtrude","CAP_FACE",FACE,{"disambiguationData":[OSD([sQuery(id+"F4.wireOp",EDGE,"E29")])],"isStart":false}),makeQuery(id+"F5.opExtrude","CAP_FACE",FACE,{"disambiguationData":[OSD([sQuery(id+"F4.wireOp",EDGE,"E30")])],"isStart":false})])],"derivedFrom":makeQuery(id+"F2.opExtrude","CAP_EDGE",EDGE,{"disambiguationData":[OSD([subQ2])],"isStart":false})});}
            var Q1;
            Q1=makeQuery(id+"F9.boolean.opBoolean","COPY",EDGE,{"derivedFrom":makeQuery(id+"F9.opExtrude","CAP_EDGE",EDGE,{"disambiguationData":[OSD([sQuery(id+"F8.wireOp",EDGE,"E37")])],"isStart":false})});
            var Q2;
            Q2=makeQuery(id+"F9.boolean.opBoolean","COPY",EDGE,{"derivedFrom":makeQuery(id+"F9.opExtrude","CAP_EDGE",EDGE,{"disambiguationData":[OSD([sQuery(id+"F8.wireOp",EDGE,"E39.0")])],"isStart":false})});
            var Q3;
            Q3=makeQuery(id+"F9.boolean.opBoolean","COPY",EDGE,{"derivedFrom":makeQuery(id+"F9.opExtrude","CAP_EDGE",EDGE,{"disambiguationData":[OSD([sQuery(id+"F8.wireOp",EDGE,"E41")])],"isStart":false})});
            var Q4;
            Q4=makeQuery(id+"F9.boolean.opBoolean","COPY",EDGE,{"derivedFrom":makeQuery(id+"F9.opExtrude","CAP_EDGE",EDGE,{"disambiguationData":[OSD([sQuery(id+"F8.wireOp",EDGE,"E40.0")])],"isStart":false})});
            var Q5;
            Q5=makeQuery(id+"F9.boolean.opBoolean","COPY",EDGE,{"derivedFrom":makeQuery(id+"F9.opExtrude","CAP_EDGE",EDGE,{"disambiguationData":[OSD([sQuery(id+"F8.wireOp",EDGE,"E40.0")])],"isStart":true})});
            var Q6;
            Q6=makeQuery(id+"F9.boolean.opBoolean","COPY",EDGE,{"derivedFrom":makeQuery(id+"F9.opExtrude","CAP_EDGE",EDGE,{"disambiguationData":[OSD([sQuery(id+"F8.wireOp",EDGE,"E37")])],"isStart":true})});
            var Q7;
            Q7=makeQuery(id+"F9.boolean.opBoolean","COPY",EDGE,{"derivedFrom":makeQuery(id+"F9.opExtrude","CAP_EDGE",EDGE,{"disambiguationData":[OSD([sQuery(id+"F8.wireOp",EDGE,"E39.0")])],"isStart":true})});
            var Q8;
            Q8=makeQuery(id+"F9.boolean.opBoolean","COPY",EDGE,{"derivedFrom":makeQuery(id+"F9.opExtrude","CAP_EDGE",EDGE,{"disambiguationData":[OSD([sQuery(id+"F8.wireOp",EDGE,"E41")])],"isStart":true})});
            fillet(context, id + "F10", {"entities" : qUnion([Q0, Q1, Q2, Q3, Q4, Q5, Q6, Q7, Q8]), "radius" : .5 * mm, "tangentPropagation" : true, "allowEdgeOverflow" : false});
        }
    });
